# Revit family: NRG
name_source: partatom
category: Air Terminals
revit_build: Autodesk Revit 2015 (Build: 20140606_1530(x64)
units: mm (PartAtom-declared; Revit-internal decimal feet)

## types (1)
- NRG
    Classification.Uniclass.Pr.Description = Fans
    Classification.Uniclass.Pr.Number = Pr_65_67_29
    Connection Radius = 63 mm
    Depth from Surface = 30 mm  [stored 0.0984252 ft]
    Description = Constant Pressure Motorised Grille Damper
    Electrical Phase = 1
    Fax Number = +44(0)2920-858-222
    IFCExportAs = IfcFanType
    Length = 155 mm  [stored 0.50853 ft]
    Manufacturer = Nuaire
    Manufacturer Name = Nuaire
    Maximum Ambient Temperature = 40 °C
    Model = NRG
    Nuaire Model Code = NRG
    Number of Connection Poles = 2
    OmniClass Number = 23-33 31 19
    OmniClass Title = Fans
    Postcode = CF83 1NA
    Revit Family Last Revised = 30/10/18
    Spigot Diameter = 125 mm  [stored 0.410105 ft]
    Telephone Number = +44(0)2920-858-200
    URL = http://www.nuaire.co.uk
    Unit Description = Constant Pressure Motorised Grille Damper
    VAT Registration Number = 877308
    Voltage = 230 V
    Warranty Period = 3 Years
    Weatherproof or Internal Only = Internal
    Weight = 0.00 kg
    Width = 155 mm  [stored 0.50853 ft]

note: [stored X ft] marks values corroborated as IEEE doubles in the binary element streams (Revit-internal decimal feet)

## geometry (parser evidence)
native form markers: Blend x24, Sweep x11
no freeform markers — native parametric forms only
